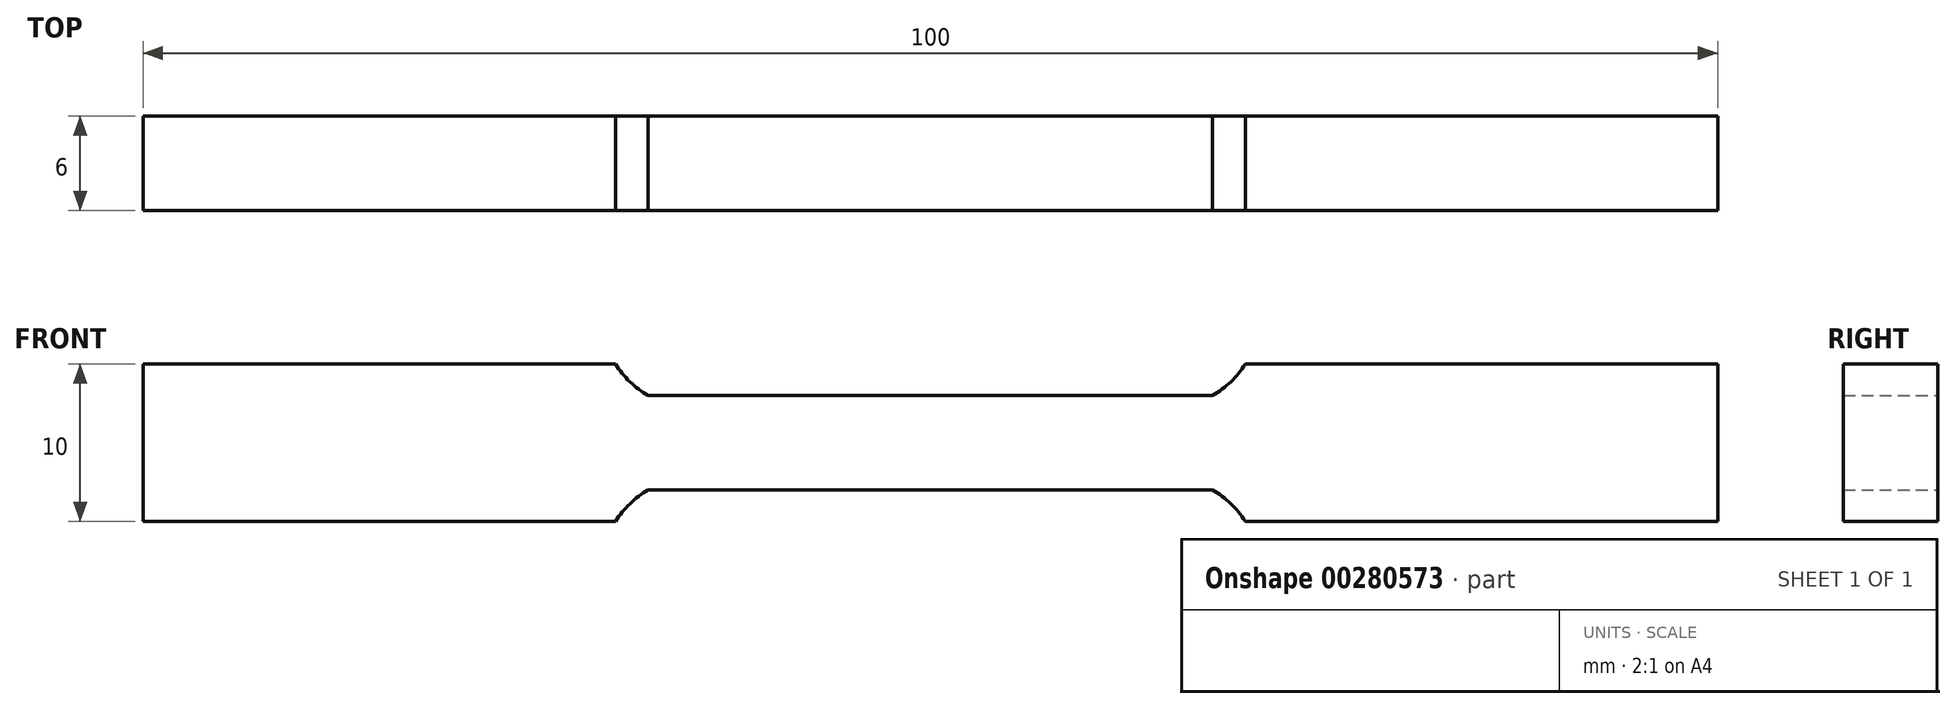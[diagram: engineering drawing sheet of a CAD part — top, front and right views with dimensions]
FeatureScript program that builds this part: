
annotation { "Feature Type Name" : "Feature", "Feature Type Description" : "" }
export const myFeature = defineFeature(function(context is Context, id is Id, definition is map)
    precondition{}
    {
        {
            var Q0;
            Q0=qCreatedBy(makeId("Front.planeOp"),FACE);
            var sketch = newSketch(context, id + "F0", { "sketchPlane" : qUnion([Q0])});
            skLineSegment(sketch, "E0", {"start": v(0, 3) * mm, "end": v(17.93, 3) * mm});
            skArc(sketch, "E1", {"start": v(17.93, 3) * mm, "mid": v(19.09, 3.87) * mm, "end": v(20, 5) * mm});
            skLineSegment(sketch, "E2", {"start": v(20, 5) * mm, "end": v(50, 5) * mm});
            skLineSegment(sketch, "E3", {"start": v(50, 5) * mm, "end": v(50, 0) * mm});
            skLineSegment(sketch, "E4.MirrorCS", {"start": v(0, -3) * mm, "end": v(17.93, -3) * mm});
            skLineSegment(sketch, "E5.MirrorCS", {"start": v(20, -5) * mm, "end": v(50, -5) * mm});
            skLineSegment(sketch, "E6.MirrorCS", {"start": v(50, -5) * mm, "end": v(50, 0) * mm});
            skArc(sketch, "E7.MirrorCS", {"start": v(17.93, -3) * mm, "mid": v(19.09, -3.87) * mm, "end": v(20, -5) * mm});
            skLineSegment(sketch, "E8.MirrorCS", {"start": v(-20, -5) * mm, "end": v(-50, -5) * mm});
            skLineSegment(sketch, "E9.MirrorCS", {"start": v(-20, 5) * mm, "end": v(-50, 5) * mm});
            skLineSegment(sketch, "E10.MirrorCS", {"start": v(-50, -5) * mm, "end": v(-50, 0) * mm});
            skLineSegment(sketch, "E11.MirrorCS", {"start": v(-50, 5) * mm, "end": v(-50, 0) * mm});
            skLineSegment(sketch, "E12.MirrorCS", {"start": v(0, 3) * mm, "end": v(-17.93, 3) * mm});
            skLineSegment(sketch, "E13.MirrorCS", {"start": v(0, -3) * mm, "end": v(-17.93, -3) * mm});
            skArc(sketch, "E14.MirrorCS", {"start": v(-17.93, 3) * mm, "mid": v(-19.09, 3.87) * mm, "end": v(-20, 5) * mm});
            skArc(sketch, "E15.MirrorCS", {"start": v(-17.93, -3) * mm, "mid": v(-19.09, -3.87) * mm, "end": v(-20, -5) * mm});
            skSolve(sketch);
        }
        {
            var Q0;
            Q0=makeQuery(id+"F0.imprint","IMPRINT",FACE,{"disambiguationData":[TD([[makeQuery(id+"F0.imprint","IMPRINT",EDGE,{"derivedFrom":sQuery(id+"F0.wireOp",EDGE,"E0")}),-1.0]])]});
            extrude(context, id + "F1", {"entities" : qUnion([Q0]), "endBound" : BoundingType.SYMMETRIC, "depth" : 6 * mm});
        }
    });
